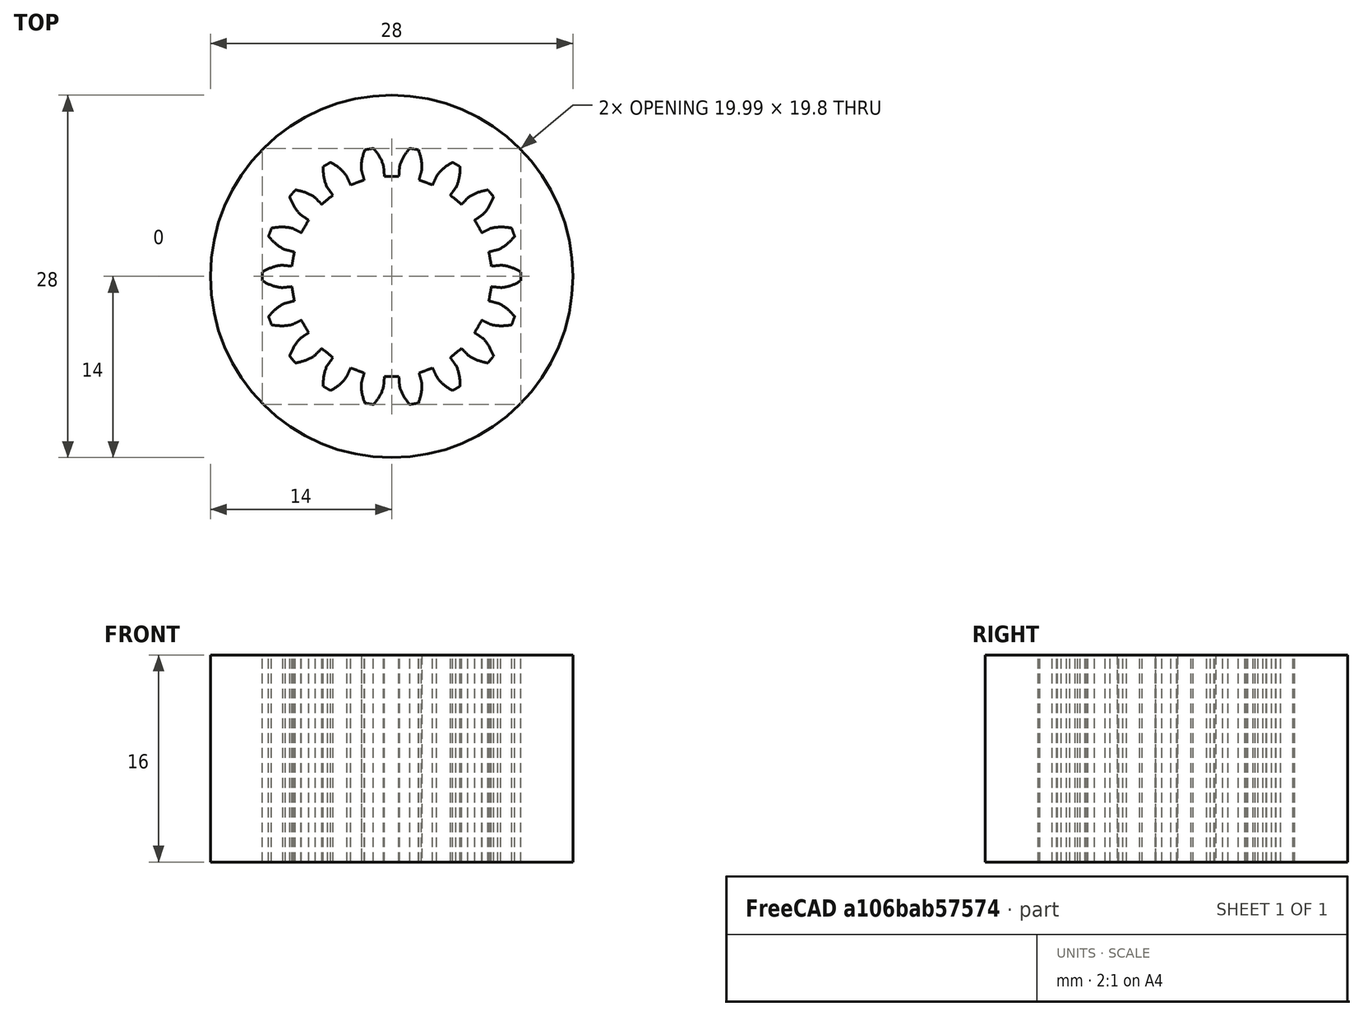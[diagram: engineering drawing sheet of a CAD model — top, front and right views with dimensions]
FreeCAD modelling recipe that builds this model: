
FCSTD DOCUMENT  (FreeCAD 0.19R24276 (Git))
Label: Gear_privod_perehodnik_to_GT2_gear_part
License: All rights reserved
LicenseURL: http://en.wikipedia.org/wiki/All_rights_reserved
objects: PartDesign::ShapeBinder×2, Sketcher::SketchObject×1, PartDesign::FeaturePython×1, PartDesign::Pad×1, Part::Cut×1, PartDesign::Body×1
note: 8 computed .brp shape members not serialized (recipe doc carries the construction recipe); baked Part::Feature solids carry a one-line shape summary decoded from their .brp

FEATURE [Sketcher::SketchObject] Sketch
  FullyConstrained = true
  MapMode = 5
  Support = -> [XY_Plane]
  sketch-geometry (1):
    g0: Circle CenterX=0 CenterY=0 CenterZ=0 NormalX=0 NormalY=0 NormalZ=1 AngleXU=0 Radius=14
  constraints (2):
    c: Coincident(g0,g-1)
    c: Diameter(g0) = 28
FEATURE [PartDesign::FeaturePython] involutegear  # WARN: FeaturePython — macro-defined, semantics opaque (R4)
  AttacherType = Attacher::AttachEngine3D
  backlash = 0
  beta = 0
  clearance = 0.25
  da = 20
  df = 15.5
  double_helix = false
  dw = 18
  head = 0
  height = 16
  module = 1
  numpoints = 6
  pressure_angle = 20
  properties_from_tool = false
  reversed_backlash = false
  shift = 0
  simple = false
  teeth = 18
  transverse_pitch = 3.14159
  undercut = false
  version = 0.0.3
FEATURE [PartDesign::Pad] Pad
  BaseFeature = -> involutegear
  Direction = (1,1,1)
  Length = 16
  Length2 = 100
  Profile = -> Sketch
  Type = 0
FEATURE [Part::Cut] Cut
  Base = -> Pad
  Tool = -> involutegear
FEATURE [PartDesign::ShapeBinder] CopyCut
  TraceSupport = false
FEATURE [PartDesign::ShapeBinder] CopyCut001
  TraceSupport = false
FEATURE [PartDesign::Body] Body
  Group = -> [Sketch,involutegear,Pad,CopyCut,CopyCut001]
  Origin = -> Origin
  Tip = -> Pad
